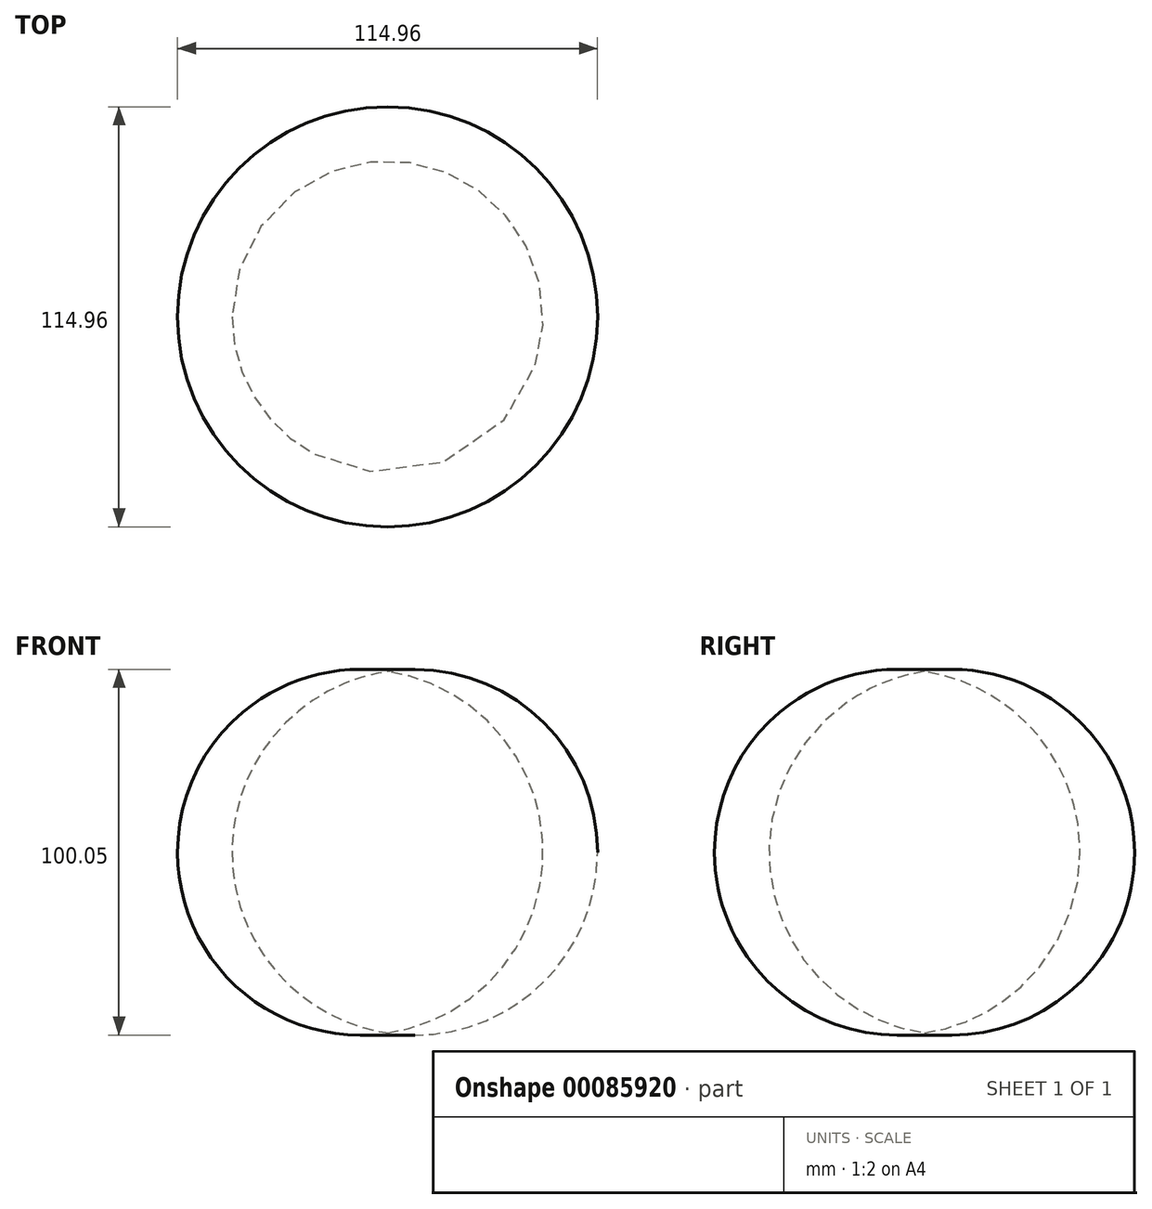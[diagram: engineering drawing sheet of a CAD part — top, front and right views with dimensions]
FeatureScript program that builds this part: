
annotation { "Feature Type Name" : "Feature", "Feature Type Description" : "" }
export const myFeature = defineFeature(function(context is Context, id is Id, definition is map)
    precondition{}
    {
        {
            var Q0;
            Q0=qCreatedBy(makeId("Front.planeOp"),FACE);
            var sketch = newSketch(context, id + "F0", { "sketchPlane" : qUnion([Q0])});
            skLineSegment(sketch, "E0", {"start": v(-32.78, 55.28) * mm, "end": v(-32.78, -43.66) * mm});
            skArc(sketch, "E1", {"start": v(-32.78, -43.66) * mm, "mid": v(9.79, 5.81) * mm, "end": v(-32.78, 55.28) * mm});
            skSolve(sketch);
        }
        {
            var Q0;
            Q0=makeQuery(id+"F0.imprint","IMPRINT",FACE,{"disambiguationData":[TD([[makeQuery(id+"F0.imprint","IMPRINT",EDGE,{"derivedFrom":sQuery(id+"F0.wireOp",EDGE,"E0")}),1.0]])]});
            var Q1;
            Q1=sQuery(id+"F0.wireOp",EDGE,"E0");
            revolve(context, id + "F1", {"entities" : qUnion([Q0]), "axis" : qUnion([Q1]), "revolveType" : RevolveType.FULL});
        }
    });
